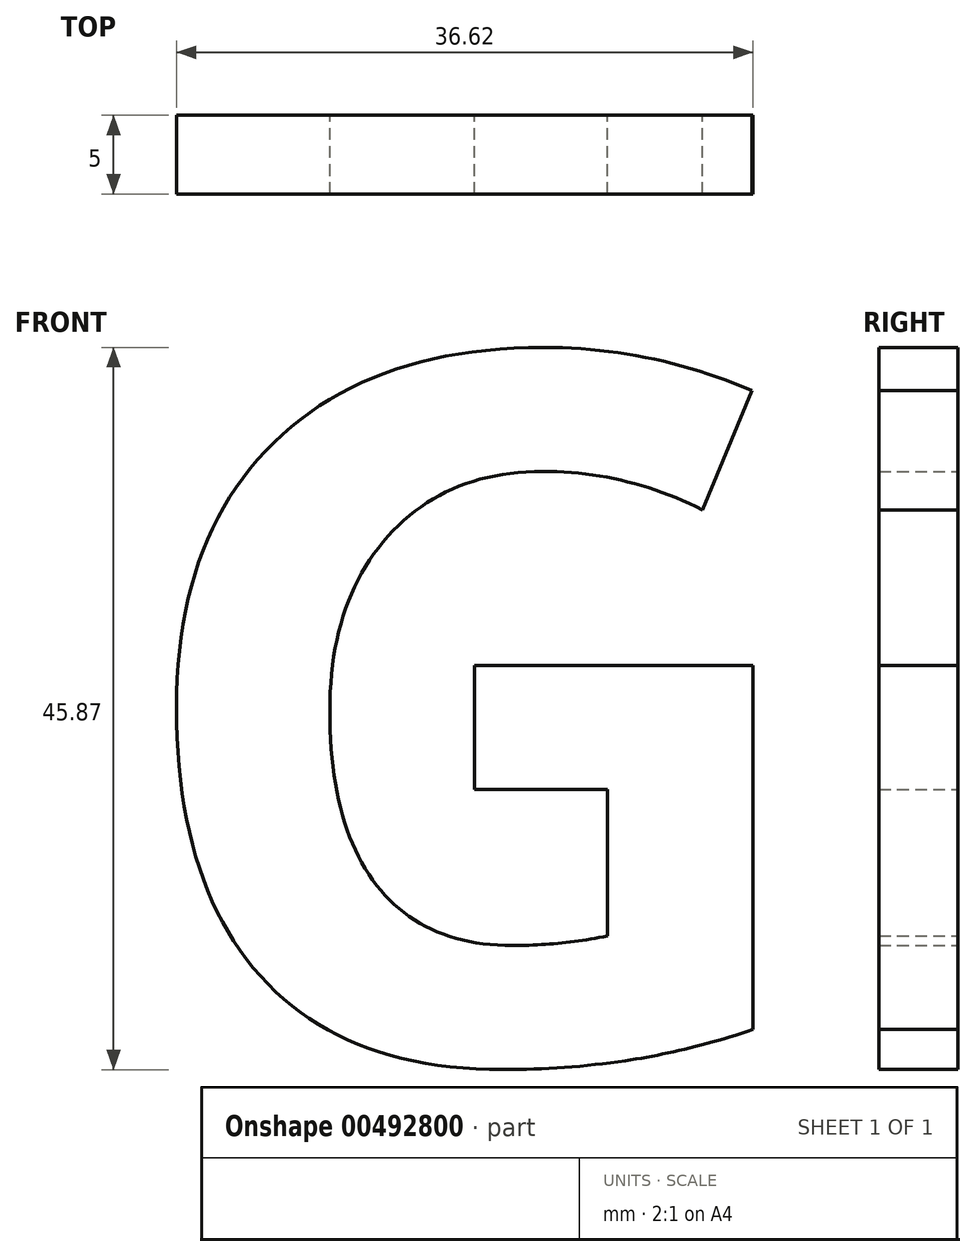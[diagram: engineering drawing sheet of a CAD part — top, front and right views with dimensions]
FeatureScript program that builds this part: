
annotation { "Feature Type Name" : "Feature", "Feature Type Description" : "" }
export const myFeature = defineFeature(function(context is Context, id is Id, definition is map)
    precondition{}
    {
        {
            var Q0;
            Q0=qCreatedBy(makeId("Front.planeOp"),FACE);
            var sketch = newSketch(context, id + "F0", { "sketchPlane" : qUnion([Q0])});
            skText(sketch, "E0", { "text": "G", "fontName": "OpenSans-Bold.ttf"});
            const initialGuessF0  = {"E0": [-0.06777, 0.02876, 1, 0, 0.045]};
            skSetInitialGuess(sketch, initialGuessF0);
            skSolve(sketch);
        }
        {
            var Q0;
            Q0=makeQuery(id+"F0.imprint","IMPRINT",FACE,{"disambiguationData":[TD([[makeQuery(id+"F0.imprint","IMPRINT",EDGE,{"derivedFrom":sQuery(id+"F0.wireOp",EDGE,"E0.sketch_text.stroke-0")}),-1.0]])]});
            extrude(context, id + "F1", {"entities" : qUnion([Q0]), "depth" : 5 * mm});
        }
    });
